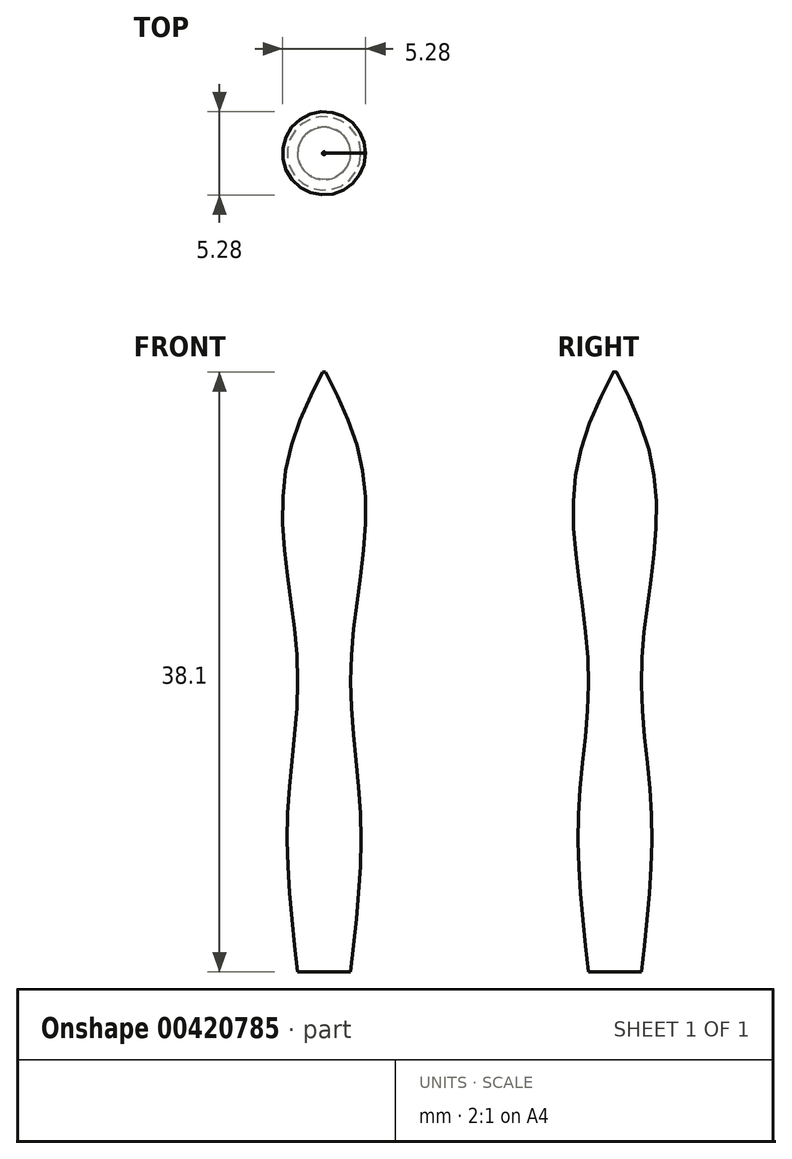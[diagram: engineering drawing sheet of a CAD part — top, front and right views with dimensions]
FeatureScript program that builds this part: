
annotation { "Feature Type Name" : "Feature", "Feature Type Description" : "" }
export const myFeature = defineFeature(function(context is Context, id is Id, definition is map)
    precondition{}
    {
        {
            var Q0;
            Q0=qCreatedBy(makeId("Top.planeOp"),FACE);
            var sketch = newSketch(context, id + "F0", { "sketchPlane" : qUnion([Q0])});
            skCircle(sketch, "E0", {"center": v(0, 0) * mm, "radius": 1.68 * mm});
            skSolve(sketch);
        }
        {
            var Q0;
            Q0=qCreatedBy(makeId("Top.planeOp"),FACE);
            cPlane(context, id + "F1", {"entities" : qUnion([Q0]), "cplaneType" : CPlaneType.OFFSET, "offset" : 38.1 * mm, "width" : 152.4 * mm, "height" : 152.4 * mm});
        }
        {
            var Q0;
            Q0=qCreatedBy(makeId("Top.planeOp"),FACE);
            cPlane(context, id + "F2", {"entities" : qUnion([Q0]), "cplaneType" : CPlaneType.OFFSET, "offset" : 19.05 * mm, "width" : 152.4 * mm, "height" : 152.4 * mm});
        }
        {
            var Q0;
            Q0=qCreatedBy(id+"F2.planeOp",FACE);
            cPlane(context, id + "F3", {"entities" : qUnion([Q0]), "cplaneType" : CPlaneType.OFFSET, "offset" : 10.16 * mm, "width" : 152.4 * mm, "height" : 152.4 * mm});
        }
        {
            var Q0;
            Q0=qCreatedBy(makeId("Top.planeOp"),FACE);
            cPlane(context, id + "F4", {"entities" : qUnion([Q0]), "cplaneType" : CPlaneType.OFFSET, "offset" : 10.16 * mm, "width" : 152.4 * mm, "height" : 152.4 * mm});
        }
        {
            var Q0;
            Q0=qCreatedBy(id+"F4.planeOp",FACE);
            var sketch = newSketch(context, id + "F5", { "sketchPlane" : qUnion([Q0])});
            skCircle(sketch, "E1", {"center": v(0, 0) * mm, "radius": 2.3 * mm});
            skSolve(sketch);
        }
        {
            var Q0;
            Q0=qCreatedBy(id+"F2.planeOp",FACE);
            var sketch = newSketch(context, id + "F6", { "sketchPlane" : qUnion([Q0])});
            skCircle(sketch, "E2", {"center": v(0, 0) * mm, "radius": 1.68 * mm});
            skSolve(sketch);
        }
        {
            var Q0;
            Q0=qCreatedBy(id+"F3.planeOp",FACE);
            var sketch = newSketch(context, id + "F7", { "sketchPlane" : qUnion([Q0])});
            skCircle(sketch, "E3", {"center": v(0, 0) * mm, "radius": 2.64 * mm});
            skSolve(sketch);
        }
        {
            var Q0;
            Q0=qCreatedBy(id+"F1.planeOp",FACE);
            var sketch = newSketch(context, id + "F8", { "sketchPlane" : qUnion([Q0])});
            skCircle(sketch, "E4", {"center": v(0, 0) * mm, "radius": 0.1 * mm});
            skSolve(sketch);
        }
        {
            var Q0;
            Q0=qCreatedBy(id+"F3.planeOp",FACE);
            cPlane(context, id + "F9", {"entities" : qUnion([Q0]), "cplaneType" : CPlaneType.OFFSET, "offset" : 3.8 * mm, "width" : 152.4 * mm, "height" : 152.4 * mm});
        }
        {
            var Q0;
            Q0=qCreatedBy(id+"F9.planeOp",FACE);
            var sketch = newSketch(context, id + "F10", { "sketchPlane" : qUnion([Q0])});
            skCircle(sketch, "E5", {"center": v(0, 0) * mm, "radius": 2.2 * mm});
            skSolve(sketch);
        }
        {
            var Q0;
            Q0 = qSketchRegion(id + "F0", true);
            var Q1;
            Q1 = qSketchRegion(id + "F5", true);
            var Q2;
            Q2 = qSketchRegion(id + "F6", true);
            var Q3;
            Q3 = qSketchRegion(id + "F7", true);
            var Q4;
            Q4 = qSketchRegion(id + "F10", true);
            var Q5;
            Q5 = qSketchRegion(id + "F8", true);
            loft(context, id + "F11", {"sheetProfilesArray" : [{ "sheetProfileEntities" : qUnion([Q0]) }, { "sheetProfileEntities" : qUnion([Q1]) }, { "sheetProfileEntities" : qUnion([Q2]) }, { "sheetProfileEntities" : qUnion([Q3]) }, { "sheetProfileEntities" : qUnion([Q4]) }, { "sheetProfileEntities" : qUnion([Q5]) }]});
        }
    });
